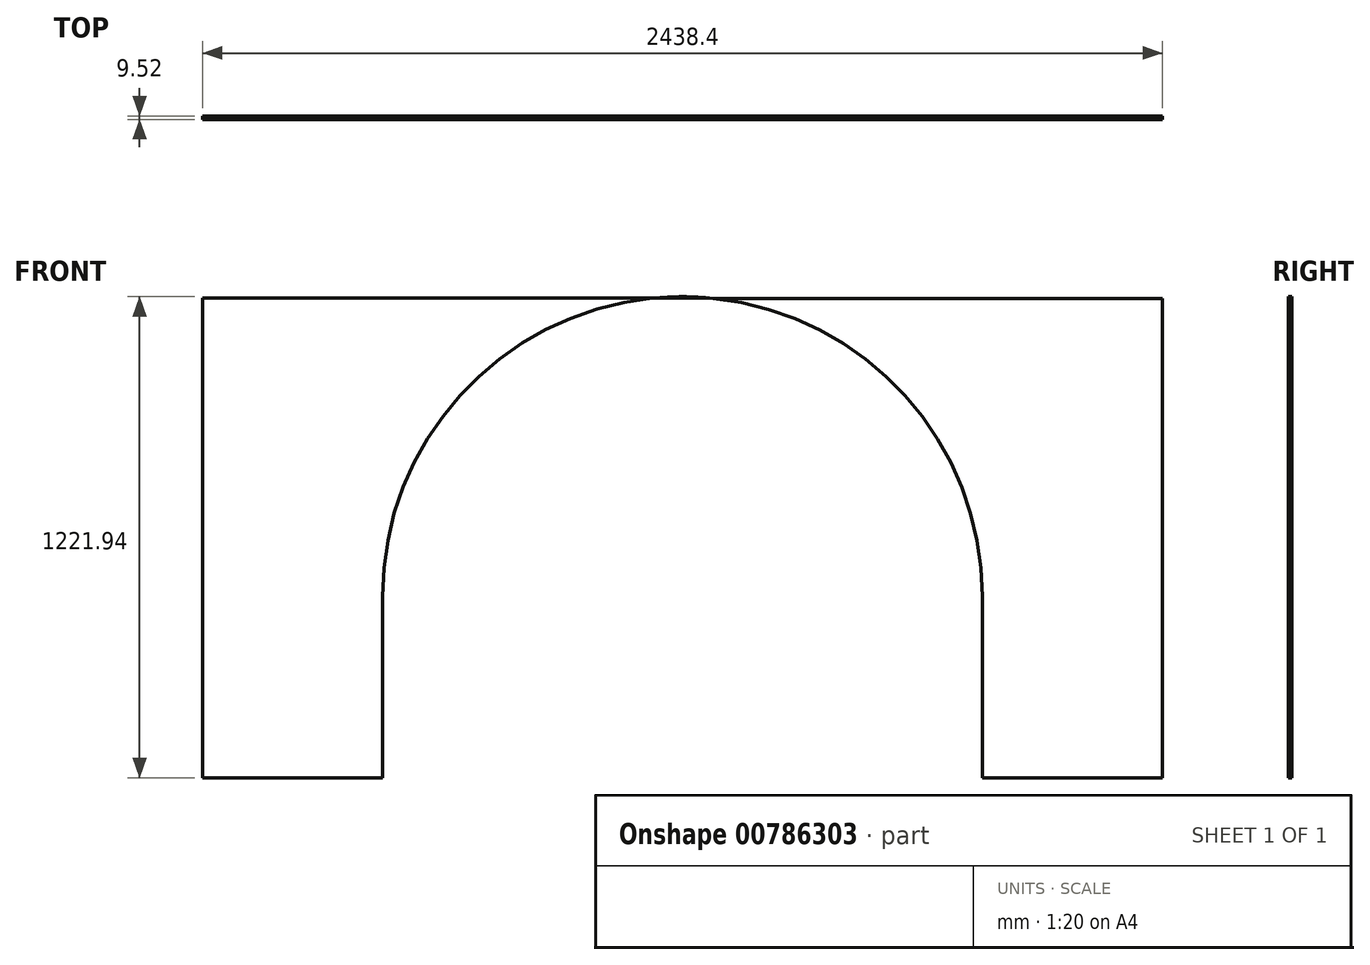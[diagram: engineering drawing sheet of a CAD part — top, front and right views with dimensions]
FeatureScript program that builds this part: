
annotation { "Feature Type Name" : "Feature", "Feature Type Description" : "" }
export const myFeature = defineFeature(function(context is Context, id is Id, definition is map)
    precondition{}
    {
        {
            var Q0;
            Q0=qCreatedBy(makeId("Front.planeOp"),FACE);
            var sketch = newSketch(context, id + "F0", { "sketchPlane" : qUnion([Q0])});
            skArc(sketch, "E0", {"start": v(-762, 0) * mm, "mid": v(0, 762) * mm, "end": v(762, 0) * mm});
            skLineSegment(sketch, "E1", {"start": v(-1219.2, -5.1) * mm, "end": v(-1219.2, 759.26) * mm});
            skLineSegment(sketch, "E2", {"start": v(-1219.2, 759.26) * mm, "end": v(1219.2, 756.9) * mm});
            skLineSegment(sketch, "E3", {"start": v(1219.2, 756.9) * mm, "end": v(1219.2, -5.1) * mm});
            skLineSegment(sketch, "E4", {"start": v(-762, 0) * mm, "end": v(-762, -459.94) * mm});
            skLineSegment(sketch, "E5", {"start": v(-762, -459.94) * mm, "end": v(-1219.2, -459.94) * mm});
            skLineSegment(sketch, "E6", {"start": v(-1219.2, -459.94) * mm, "end": v(-1219.2, -5.1) * mm});
            skLineSegment(sketch, "E7", {"start": v(762, 0) * mm, "end": v(762, -459.94) * mm});
            skLineSegment(sketch, "E8", {"start": v(762, -459.94) * mm, "end": v(1219.2, -459.94) * mm});
            skLineSegment(sketch, "E9", {"start": v(1219.2, -459.94) * mm, "end": v(1219.2, -5.1) * mm});
            skSolve(sketch);
        }
        {
            var Q0;
            {var subQ1=sQuery(id+"F0.wireOp",EDGE,"E1");Q0=makeQuery(id+"F0.imprint","IMPRINT",FACE,{"disambiguationData":[TD([[makeQuery(id+"F0.imprint","IMPRINT",EDGE,{"derivedFrom":subQ1}),-1.0]])]});}
            var Q1;
            {var subQ1=sQuery(id+"F0.wireOp",EDGE,"E3");Q1=makeQuery(id+"F0.imprint","IMPRINT",FACE,{"disambiguationData":[TD([[makeQuery(id+"F0.imprint","IMPRINT",EDGE,{"derivedFrom":subQ1}),-1.0]])]});}
            var Q2;
            Q2 = qSketchRegion(id + "F0", true);
            extrude(context, id + "F1", {"entities" : qUnion([Q0, Q1, Q2]), "endBound" : BoundingType.SYMMETRIC, "depth" : 9.52 * mm, "offsetDistance" : 25.4 * mm});
        }
    });
